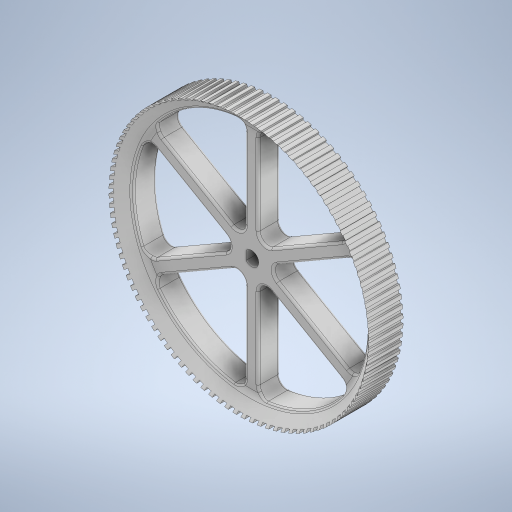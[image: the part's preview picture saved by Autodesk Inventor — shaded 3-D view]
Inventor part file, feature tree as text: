
AUTODESK INVENTOR PART (.ipt)
format: ipt  version: 2024.2 (Build 282272000, 272)  size: 1,238,528 bytes
history: native  units: mm
features: fillet x4, sketch x3, extrude x2, revolve x1, chamfer x1
ambient origin geometry x8: Origin, YZ Plane, XZ Plane, XY Plane, X Axis, Y Axis, Z Axis, Center Point
bodies: Solid1 (feature_tree)
feature tree (11):
  revolve  "Revolution1"  [1 undecoded]
  extrude  "Extrusion1"  Depth=30.0mm
  extrude  "Extrusion2"  Depth=0.5mm
  fillet  "Fillet1"  Radius=1.0mm
  fillet  "Fillet2"  Radius=1.0mm
  fillet  "Fillet3"  Radius=1000.0mm
  fillet  "Fillet4"  Radius=10.0mm
  chamfer  "Chamfer1"  Distance=3.25mm
  sketch  "Sketch1"  dims[d0=3.0mm d1=8.0mm]
  sketch  "Sketch2"  dims[d2=5.0mm d3=30.0mm]
  sketch  "Sketch3"  dims[d4=90.0deg d6=0.5mm d7=1.0mm d8=1.0mm d9=1000.0mm d11=360.0deg d13=10.0mm d14=0.0mm d15=3.25mm d16=2.9mm d17=7.0mm d18=3.0mm d19=1.5mm d20=60.0mm d22=360.0deg d24=5.0mm d25=0.0mm d26=2.0mm d27=2.0mm d28=0.5mm d29=0.5mm d30=0.4mm d31=2.0mm d32=45.0deg]
note: 1 required parameter value undecoded (feature->parameter linkage not recoverable at this tier; creation-order binding heuristic only, values carry confidence <= 0.55)
